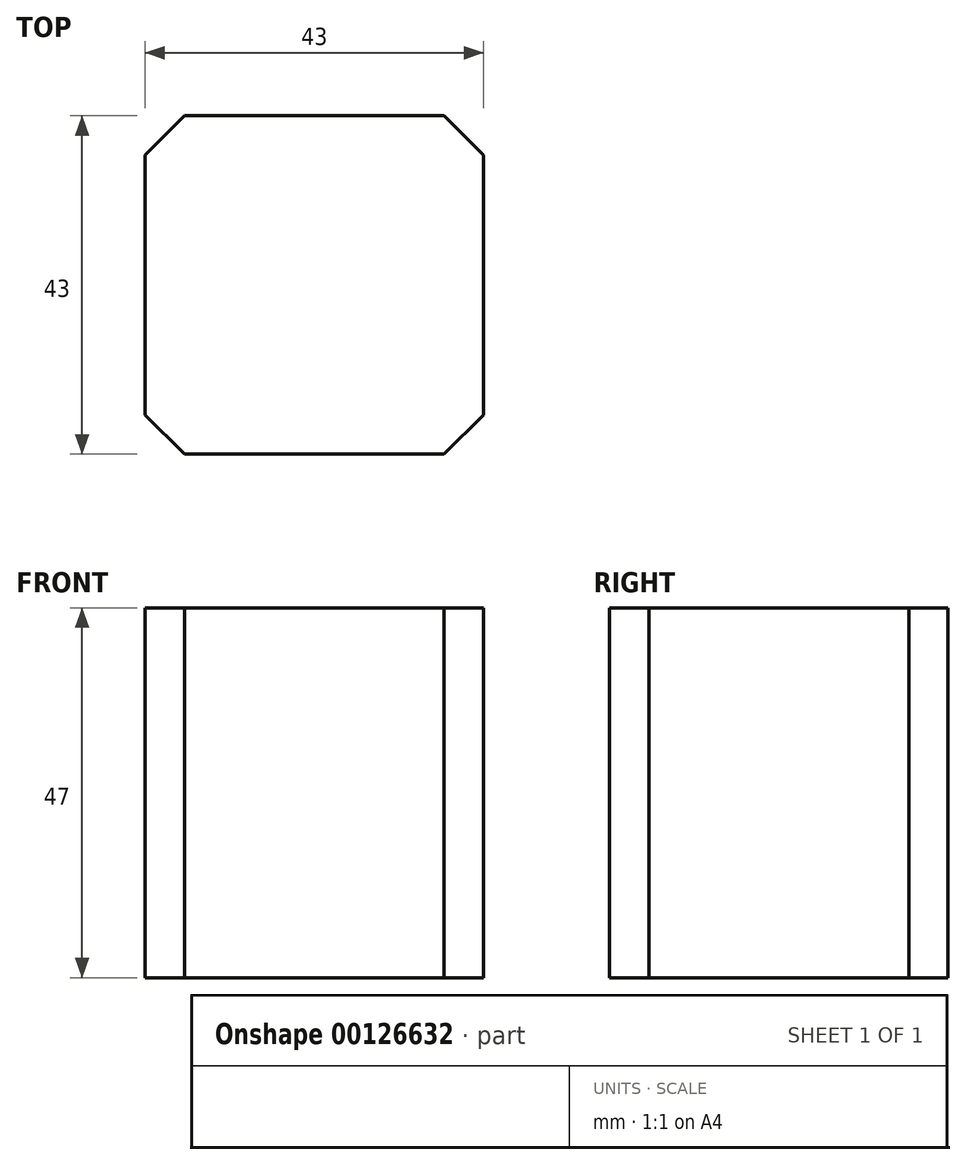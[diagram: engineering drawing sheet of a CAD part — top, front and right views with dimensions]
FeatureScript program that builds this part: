
annotation { "Feature Type Name" : "Feature", "Feature Type Description" : "" }
export const myFeature = defineFeature(function(context is Context, id is Id, definition is map)
    precondition{}
    {
        {
            var Q0;
            Q0=qCreatedBy(makeId("Top.planeOp"),FACE);
            var sketch = newSketch(context, id + "F0", { "sketchPlane" : qUnion([Q0])});
            skLineSegment(sketch, "E0.bottom", {"start": v(-22.55, 18.92) * mm, "end": v(20.45, 18.92) * mm});
            skLineSegment(sketch, "E0.top", {"start": v(-22.55, -24.08) * mm, "end": v(20.45, -24.08) * mm});
            skLineSegment(sketch, "E0.left", {"start": v(-22.55, 18.92) * mm, "end": v(-22.55, -24.08) * mm});
            skLineSegment(sketch, "E0.right", {"start": v(20.45, 18.92) * mm, "end": v(20.45, -24.08) * mm});
            skSolve(sketch);
        }
        {
            var Q0;
            Q0=makeQuery(id+"F0.imprint","IMPRINT",FACE,{"disambiguationData":[TD([[makeQuery(id+"F0.imprint","IMPRINT",EDGE,{"derivedFrom":sQuery(id+"F0.wireOp",EDGE,"E0.bottom")}),-1.0]])]});
            extrude(context, id + "F1", {"entities" : qUnion([Q0]), "depth" : 47 * mm});
        }
        {
            var Q0;
            Q0=makeQuery(id+"F1.opExtrude","SWEPT_EDGE",EDGE,{"disambiguationData":[OSD([sQuery(id+"F0.wireOp",EDGE,"E0.top"),sQuery(id+"F0.wireOp",EDGE,"E0.right")])]});
            var Q1;
            Q1=makeQuery(id+"F1.opExtrude","SWEPT_EDGE",EDGE,{"disambiguationData":[OSD([sQuery(id+"F0.wireOp",EDGE,"E0.top"),sQuery(id+"F0.wireOp",EDGE,"E0.left")])]});
            var Q2;
            Q2=makeQuery(id+"F1.opExtrude","SWEPT_EDGE",EDGE,{"disambiguationData":[OSD([sQuery(id+"F0.wireOp",EDGE,"E0.bottom"),sQuery(id+"F0.wireOp",EDGE,"E0.right")])]});
            var Q3;
            Q3=makeQuery(id+"F1.opExtrude","SWEPT_EDGE",EDGE,{"disambiguationData":[OSD([sQuery(id+"F0.wireOp",EDGE,"E0.bottom"),sQuery(id+"F0.wireOp",EDGE,"E0.left")])]});
            chamfer(context, id + "F2", {"entities" : qUnion([Q0, Q1, Q2, Q3]), "width" : 5 * mm, "tangentPropagation" : true});
        }
    });
